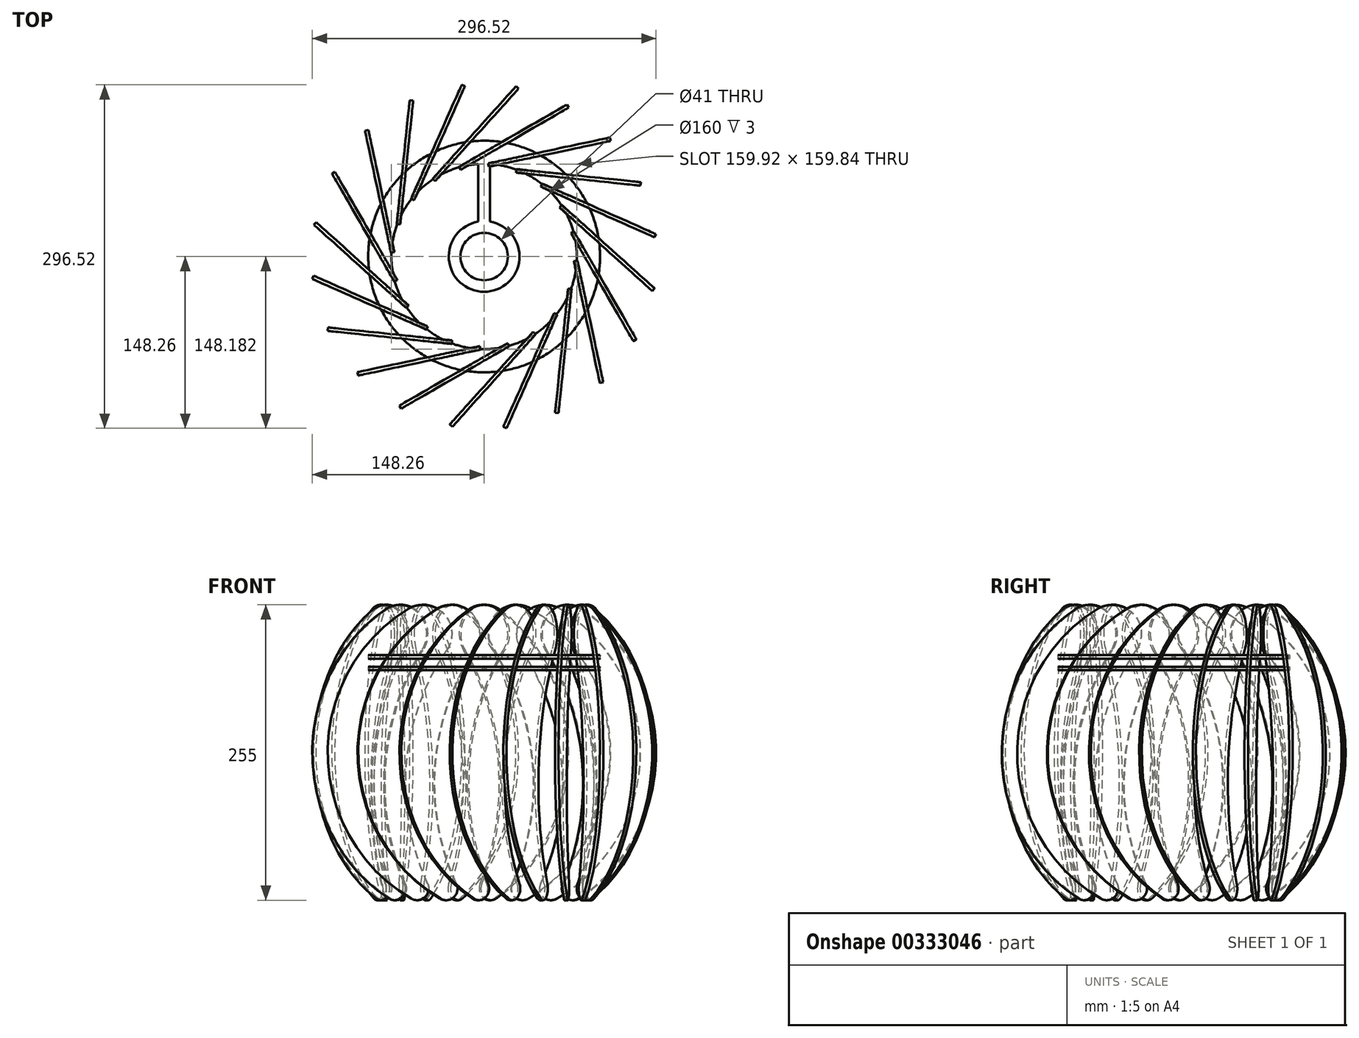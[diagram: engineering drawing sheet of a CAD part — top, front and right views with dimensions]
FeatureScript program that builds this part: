
annotation { "Feature Type Name" : "Feature", "Feature Type Description" : "" }
export const myFeature = defineFeature(function(context is Context, id is Id, definition is map)
    precondition{}
    {
        {
            assignVariable(context, id + "F0", {"name" : "antal", "anyValue" : 20});
        }
        {
            assignVariable(context, id + "F1", {"name" : "tykkelse", "anyValue" : 3});
        }
        {
            var Q0;
            Q0=qCreatedBy(makeId("Top.planeOp"),FACE);
            var sketch = newSketch(context, id + "F2", { "sketchPlane" : qUnion([Q0])});
            skCircle(sketch, "E0", {"center": v(0, 0) * mm, "radius": 100 * mm});
            skCircle(sketch, "E1", {"center": v(0, 0) * mm, "radius": 80 * mm});
            skSolve(sketch);
        }
        {
            var Q0;
            Q0=makeQuery(id+"F2.imprint","IMPRINT",FACE,{"disambiguationData":[TD([[makeQuery(id+"F2.imprint","IMPRINT",EDGE,{"derivedFrom":sQuery(id+"F2.wireOp",EDGE,"E0")}),1.0]])]});
            extrude(context, id + "F3", {"entities" : qUnion([Q0]), "endBound" : BoundingType.SYMMETRIC, "depth" : 3 * mm});
        }
        {
            var Q0;
            Q0=qCreatedBy(makeId("Top.planeOp"),FACE);
            var sketch = newSketch(context, id + "F4", { "sketchPlane" : qUnion([Q0])});
            skCircle(sketch, "E2", {"center": v(0, 0) * mm, "radius": 20.5 * mm});
            skCircle(sketch, "E3", {"center": v(0, 0) * mm, "radius": 30.5 * mm});
            skSolve(sketch);
        }
        {
            var Q0;
            Q0=qCreatedBy(makeId("Top.planeOp"),FACE);
            var sketch = newSketch(context, id + "F5", { "sketchPlane" : qUnion([Q0])});
            skLineSegment(sketch, "E4.bottom", {"start": v(5, 21.5) * mm, "end": v(-5, 21.5) * mm});
            skLineSegment(sketch, "E4.top", {"start": v(5, 83) * mm, "end": v(-5, 83) * mm});
            skLineSegment(sketch, "E4.left", {"start": v(5, 21.5) * mm, "end": v(5, 83) * mm});
            skLineSegment(sketch, "E4.right", {"start": v(-5, 21.5) * mm, "end": v(-5, 83) * mm});
            skPoint(sketch, "E4.middle", {"position": v(0, 52.25) * mm});
            skSolve(sketch);
        }
        {
            var Q0;
            Q0=makeQuery(id+"F4.imprint","IMPRINT",FACE,{"disambiguationData":[TD([[makeQuery(id+"F4.imprint","IMPRINT",EDGE,{"derivedFrom":sQuery(id+"F4.wireOp",EDGE,"E2")}),-1.0]])]});
            var Q1;
            Q1=makeQuery(id+"FtXXHpX7dejrLfR_1.1.F5.imprint","IMPRINT",FACE,{"disambiguationData":[TD([[makeQuery(id+"FtXXHpX7dejrLfR_1.1.F5.imprint","IMPRINT",EDGE,{"derivedFrom":sQuery(id+"FtXXHpX7dejrLfR_1.1.F5.wireOp",EDGE,"E4.bottom")}),-1.0]])]});
            var Q2;
            Q2=makeQuery(id+"F5.imprint","IMPRINT",FACE,{"disambiguationData":[TD([[makeQuery(id+"F5.imprint","IMPRINT",EDGE,{"derivedFrom":sQuery(id+"F5.wireOp",EDGE,"E4.bottom")}),-1.0]])]});
            var Q3;
            Q3=makeQuery(id+"FtXXHpX7dejrLfR_1.2.F5.imprint","IMPRINT",FACE,{"disambiguationData":[TD([[makeQuery(id+"FtXXHpX7dejrLfR_1.2.F5.imprint","IMPRINT",EDGE,{"derivedFrom":sQuery(id+"FtXXHpX7dejrLfR_1.2.F5.wireOp",EDGE,"E4.bottom")}),-1.0]])]});
            var Q4;
            Q4=makeQuery(id+"FtXXHpX7dejrLfR_1.3.F5.imprint","IMPRINT",FACE,{"disambiguationData":[TD([[makeQuery(id+"FtXXHpX7dejrLfR_1.3.F5.imprint","IMPRINT",EDGE,{"derivedFrom":sQuery(id+"FtXXHpX7dejrLfR_1.3.F5.wireOp",EDGE,"E4.bottom")}),-1.0]])]});
            var Q5;
            Q5=makeQuery(id+"FtXXHpX7dejrLfR_1.4.F5.imprint","IMPRINT",FACE,{"disambiguationData":[TD([[makeQuery(id+"FtXXHpX7dejrLfR_1.4.F5.imprint","IMPRINT",EDGE,{"derivedFrom":sQuery(id+"FtXXHpX7dejrLfR_1.4.F5.wireOp",EDGE,"E4.bottom")}),-1.0]])]});
            extrude(context, id + "F6", {"entities" : qUnion([Q0, Q1, Q2, Q3, Q4, Q5]), "operationType" : NewBodyOperationType.ADD, "endBound" : BoundingType.SYMMETRIC, "depth" : (getVariable(context, 'tykkelse')) * mm});
        }
        {
            var Q0;
            Q0=qCreatedBy(makeId("Top.planeOp"),FACE);
            cPlane(context, id + "F7", {"entities" : qUnion([Q0]), "cplaneType" : CPlaneType.OFFSET, "offset" : 10 * mm, "oppositeDirection" : true, "width" : 150 * mm, "height" : 150 * mm});
        }
        {
            var Q0;
            Q0=qCreatedBy(id+"F7.planeOp",FACE);
            var sketch = newSketch(context, id + "F8", { "sketchPlane" : qUnion([Q0])});
            skPoint(sketch, "E5.0", {"position": v(-5, 79.84) * mm});
            skCircle(sketch, "E6.0", {"center": v(0, 0) * mm, "radius": 100 * mm});
            skCircle(sketch, "E7", {"center": v(0, 0) * mm, "radius": 80 * mm});
            skSolve(sketch);
        }
        {
            var Q0;
            Q0 = qSketchRegion(id + "F8", true);
            extrude(context, id + "F9", {"entities" : qUnion([Q0]), "endBound" : BoundingType.SYMMETRIC, "depth" : 3 * mm});
        }
        {
            var Q0;
            Q0=qCreatedBy(makeId("Top.planeOp"),FACE);
            var sketch = newSketch(context, id + "F10", { "sketchPlane" : qUnion([Q0])});
            skLineSegment(sketch, "E8", {"start": v(0, 90) * mm, "end": v(1.5, 87.4) * mm});
            skLineSegment(sketch, "E9", {"start": v(1.5, 87.4) * mm, "end": v(36.14, 107.4) * mm});
            skLineSegment(sketch, "E10", {"start": v(36.14, 107.4) * mm, "end": v(34.64, 110) * mm});
            skLineSegment(sketch, "E11", {"start": v(0, 90) * mm, "end": v(34.64, 110) * mm});
            skLineSegment(sketch, "E12", {"start": v(0, 100) * mm, "end": v(0, 80) * mm, "construction": true});
            skCircle(sketch, "E13.0.0", {"center": v(0, 0) * mm, "radius": 100 * mm, "construction": true});
            skCircle(sketch, "E14.0", {"center": v(0, 0) * mm, "radius": 80 * mm, "construction": true});
            skPoint(sketch, "E15", {"position": v(0, 90) * mm});
            skSolve(sketch);
        }
        {
            var Q0;
            Q0=makeQuery(id+"F10.imprint","IMPRINT",FACE,{"disambiguationData":[TD([[makeQuery(id+"F10.imprint","IMPRINT",EDGE,{"derivedFrom":sQuery(id+"F10.wireOp",EDGE,"E8")}),1.0]])]});
            extrude(context, id + "F11", {"entities" : qUnion([Q0]), "operationType" : NewBodyOperationType.REMOVE, "endBound" : BoundingType.THROUGH_ALL, "depth" : 25 * mm, "hasSecondDirection" : true, "secondDirectionBound" : SecondDirectionBoundingType.THROUGH_ALL, "secondDirectionOppositeDirection" : true, "secondDirectionDepth" : 25 * mm});
        }
        {
            var Q0;
            {var subQ0=sQuery(id+"F8.wireOp",EDGE,"E6.0");Q0=makeQuery(id+"F11.boolean.opBoolean","COPY",FACE,{"disambiguationData":[TD([makeQuery(id+"F9.opExtrude","SWEPT_FACE",FACE,{"disambiguationData":[OSD([subQ0])]})])],"derivedFrom":makeQuery(id+"F11.opExtrude","SWEPT_FACE",FACE,{"disambiguationData":[OSD([sQuery(id+"F10.wireOp",EDGE,"E11")])]})});}
            var sketch = newSketch(context, id + "F12", { "sketchPlane" : qUnion([Q0])});
            skArc(sketch, "E16", {"start": v(58.05, 41.32) * mm, "mid": v(26.89, 37.23) * mm, "end": v(24.35, 5.9) * mm});
            skCircle(sketch, "E17", {"center": v(50, -200) * mm, "radius": 10 * mm});
            skArc(sketch, "E18.trimOffspring", {"start": v(40.93, -195.78) * mm, "mid": v(59.9, -102.94) * mm, "end": v(35, -11.5) * mm});
            skArc(sketch, "E19.trimOffspring", {"start": v(55.01, -208.65) * mm, "mid": v(127.58, -84.53) * mm, "end": v(58.05, 41.32) * mm});
            skArc(sketch, "E20.trimOffspring", {"start": v(33.34, -8.5) * mm, "mid": v(31.3, -4.98) * mm, "end": v(29.18, -1.5) * mm});
            skArc(sketch, "E21.trimOffspring", {"start": v(27.28, 1.5) * mm, "mid": v(25.83, 3.71) * mm, "end": v(24.35, 5.9) * mm});
            skLineSegment(sketch, "E22.0", {"start": v(45, -8.5) * mm, "end": v(45, -11.5) * mm});
            skLineSegment(sketch, "E23", {"start": v(45, -8.5) * mm, "end": v(33.34, -8.5) * mm});
            skLineSegment(sketch, "E24", {"start": v(35, -11.5) * mm, "end": v(45, -11.5) * mm});
            skLineSegment(sketch, "E25.0", {"start": v(45, 1.5) * mm, "end": v(45, -1.5) * mm});
            skLineSegment(sketch, "E26", {"start": v(45, 1.5) * mm, "end": v(27.28, 1.5) * mm});
            skLineSegment(sketch, "E27", {"start": v(45, -1.5) * mm, "end": v(29.18, -1.5) * mm});
            skSolve(sketch);
        }
        {
            var Q0;
            Q0 = qSketchRegion(id + "F12", true);
            extrude(context, id + "F13", {"entities" : qUnion([Q0]), "depth" : (getVariable(context, 'tykkelse')) * mm});
        }
        {
            var Q0;
            Q0=makeQuery(id+"F13.opExtrude","SWEPT_BODY",BODY,{"disambiguationData":[OSD([sQuery(id+"F12.wireOp",EDGE,"E16"),sQuery(id+"F12.wireOp",EDGE,"E17"),sQuery(id+"F12.wireOp",EDGE,"E18.trimOffspring"),sQuery(id+"F12.wireOp",EDGE,"E19.trimOffspring"),sQuery(id+"F12.wireOp",EDGE,"c53549a4-e4b3-432d-a0ec-0fb6de3187b9.0"),sQuery(id+"F12.wireOp",EDGE,"yQ3qvXJn-M92F-mW3v-spys-oJAnTGsknceh"),sQuery(id+"F12.wireOp",EDGE,"45GGtcFT-g08S-MEPe-lEnV-MP53HY77IKTk"),sQuery(id+"F12.wireOp",EDGE,"E20.trimOffspring"),sQuery(id+"F12.wireOp",EDGE,"d5da217f-9d56-4b02-b9a9-69c4808102c5.0"),sQuery(id+"F12.wireOp",EDGE,"hG8eRuad-eHcU-Tj2M-FnlB-jMRelVOcOaA4"),sQuery(id+"F12.wireOp",EDGE,"00b5Xzf1-RX8x-temT-fXXf-5qI60aelsdhK"),sQuery(id+"F12.wireOp",EDGE,"E21.trimOffspring")])]});
            var Q1;
            Q1=makeQuery(id+"F6.opExtrude","CAP_EDGE",EDGE,{"disambiguationData":[OSD([sQuery(id+"F4.wireOp",EDGE,"E2")])],"isStart":false});
            circularPattern(context, id + "F14", {"entities" : qUnion([Q0]), "axis" : qUnion([Q1]), "angle" : 360 * degree, "instanceCount" : getVariable(context, 'antal'), "equalSpace" : true});
        }
    });
